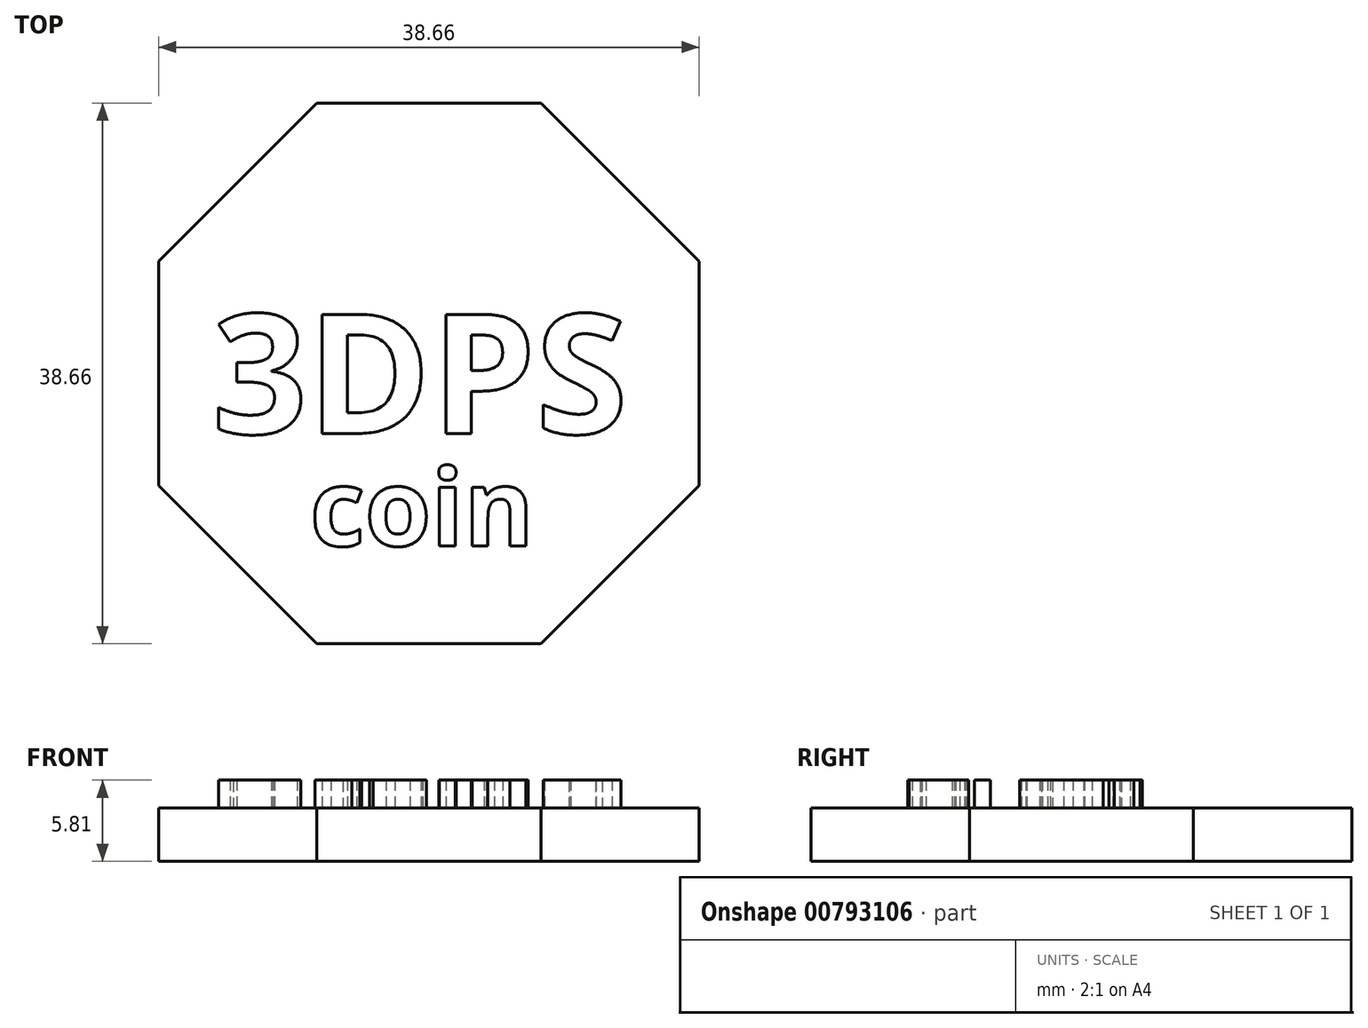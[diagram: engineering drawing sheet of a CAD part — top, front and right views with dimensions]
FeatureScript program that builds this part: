
annotation { "Feature Type Name" : "Feature", "Feature Type Description" : "" }
export const myFeature = defineFeature(function(context is Context, id is Id, definition is map)
    precondition{}
    {
        {
            var Q0;
            Q0=qCreatedBy(makeId("Top.planeOp"),FACE);
            var sketch = newSketch(context, id + "F0", { "sketchPlane" : qUnion([Q0])});
            skCircle(sketch, "E0.cCircle", {"center": v(0, 0) * mm, "radius": 19.33 * mm, "construction": true});
            skLineSegment(sketch, "E0.0", {"start": v(8, -19.33) * mm, "end": v(-8, -19.33) * mm});
            skLineSegment(sketch, "E0.1", {"start": v(-8, -19.33) * mm, "end": v(-19.33, -8) * mm});
            skLineSegment(sketch, "E0.2", {"start": v(-19.33, -8) * mm, "end": v(-19.33, 8) * mm});
            skLineSegment(sketch, "E0.3", {"start": v(-19.33, 8) * mm, "end": v(-8, 19.33) * mm});
            skLineSegment(sketch, "E0.4", {"start": v(-8, 19.33) * mm, "end": v(8, 19.33) * mm});
            skLineSegment(sketch, "E0.5", {"start": v(8, 19.33) * mm, "end": v(19.33, 8) * mm});
            skLineSegment(sketch, "E0.6", {"start": v(19.33, 8) * mm, "end": v(19.33, -8) * mm});
            skLineSegment(sketch, "E0.7", {"start": v(19.33, -8) * mm, "end": v(8, -19.33) * mm});
            skPoint(sketch, "E0.0.midPoint", {"position": v(0, -19.33) * mm});
            skSolve(sketch);
        }
        {
            var Q0;
            Q0 = qSketchRegion(id + "F0", true);
            extrude(context, id + "F1", {"entities" : qUnion([Q0]), "depth" : 3.8 * mm, "offsetDistance" : 25.4 * mm});
        }
        {
            var Q0;
            Q0=makeQuery(id+"F1.opExtrude","CAP_FACE",FACE,{"disambiguationData":[OSD([sQuery(id+"F0.wireOp",EDGE,"E0.0"),sQuery(id+"F0.wireOp",EDGE,"E0.1"),sQuery(id+"F0.wireOp",EDGE,"E0.2"),sQuery(id+"F0.wireOp",EDGE,"E0.3"),sQuery(id+"F0.wireOp",EDGE,"E0.4"),sQuery(id+"F0.wireOp",EDGE,"E0.5"),sQuery(id+"F0.wireOp",EDGE,"E0.6"),sQuery(id+"F0.wireOp",EDGE,"E0.7")])],"isStart":false});
            var sketch = newSketch(context, id + "F2", { "sketchPlane" : qUnion([Q0])});
            skCircle(sketch, "E1.cCircle", {"center": v(0, 0) * mm, "radius": 15.67 * mm, "construction": true});
            skLineSegment(sketch, "E1.0", {"start": v(-6.5, 15.67) * mm, "end": v(6.5, 15.67) * mm});
            skLineSegment(sketch, "E1.1", {"start": v(6.5, 15.67) * mm, "end": v(15.67, 6.5) * mm});
            skLineSegment(sketch, "E1.2", {"start": v(15.67, 6.5) * mm, "end": v(15.67, -6.5) * mm});
            skLineSegment(sketch, "E1.3", {"start": v(15.67, -6.5) * mm, "end": v(6.5, -15.67) * mm});
            skLineSegment(sketch, "E1.4", {"start": v(6.5, -15.67) * mm, "end": v(-6.5, -15.67) * mm});
            skLineSegment(sketch, "E1.5", {"start": v(-6.5, -15.67) * mm, "end": v(-15.67, -6.5) * mm});
            skLineSegment(sketch, "E1.6", {"start": v(-15.67, -6.5) * mm, "end": v(-15.67, 6.5) * mm});
            skLineSegment(sketch, "E1.7", {"start": v(-15.67, 6.5) * mm, "end": v(-6.5, 15.67) * mm});
            skPoint(sketch, "E1.0.midPoint", {"position": v(0, 15.67) * mm});
            skSolve(sketch);
        }
        {
            var Q0;
            Q0=makeQuery(id+"F2.imprint","IMPRINT",FACE,{"disambiguationData":[TD([[makeQuery(id+"F2.imprint","IMPRINT",EDGE,{"derivedFrom":sQuery(id+"F2.wireOp",EDGE,"E1.0")}),-1.0]])]});
            var sketch = newSketch(context, id + "F3", { "sketchPlane" : qUnion([Q0])});
            skText(sketch, "E2", { "text": "3DPS\n", "fontName": "OpenSans-Bold.ttf"});
            const initialGuessF3  = {"E2": [-0.0155, -0.0043, 1, 0, 0.00859]};
            skSetInitialGuess(sketch, initialGuessF3);
            skSolve(sketch);
        }
        {
            var Q0;
            Q0=makeQuery(id+"F2.imprint","IMPRINT",FACE,{"disambiguationData":[TD([[makeQuery(id+"F2.imprint","IMPRINT",EDGE,{"derivedFrom":sQuery(id+"F2.wireOp",EDGE,"E1.0")}),-1.0]])]});
            var sketch = newSketch(context, id + "F4", { "sketchPlane" : qUnion([Q0])});
            skText(sketch, "E3", { "text": "coin", "fontName": "OpenSans-Bold.ttf"});
            const initialGuessF4  = {"E3": [-0.0085, -0.01233, 1, 0, 0.0055]};
            skSetInitialGuess(sketch, initialGuessF4);
            skSolve(sketch);
        }
        {
            var Q0;
            Q0 = qSketchRegion(id + "F3", true);
            var Q1;
            Q1 = qSketchRegion(id + "F4", true);
            extrude(context, id + "F5", {"entities" : qUnion([Q0, Q1]), "operationType" : NewBodyOperationType.ADD, "depth" : 2 * mm, "offsetDistance" : 25 * mm});
        }
    });
